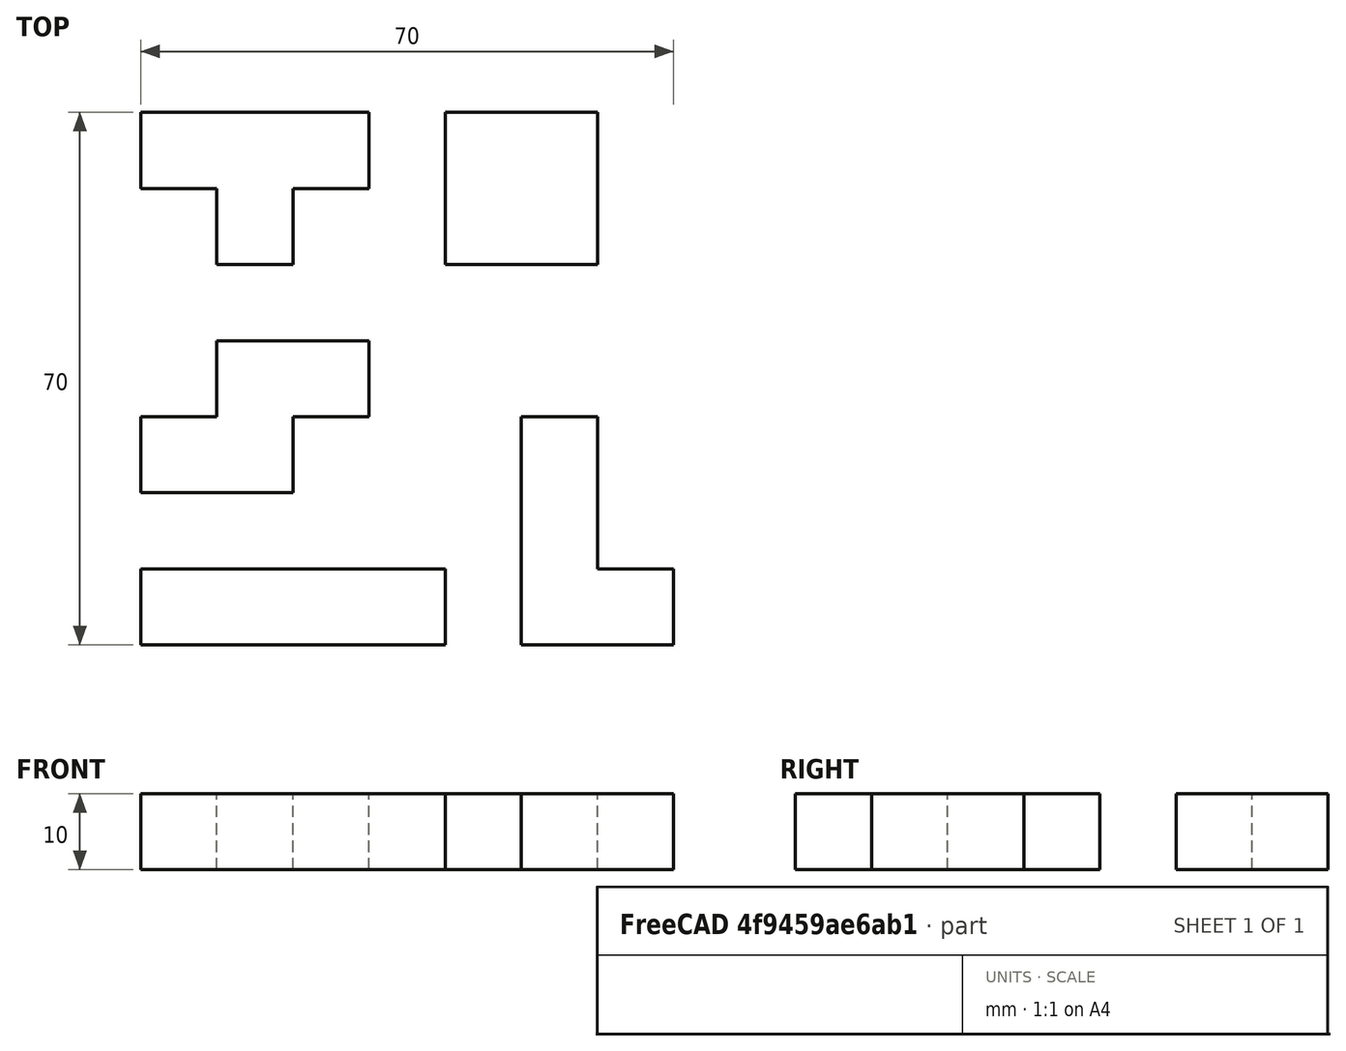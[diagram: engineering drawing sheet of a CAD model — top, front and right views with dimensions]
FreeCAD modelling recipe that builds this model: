
FCSTD DOCUMENT  (FreeCAD 1.0R39285 (Git))
Label: ojt1_t05r03_tetris
License: All rights reserved
objects: Part::Box×20, Part::MultiFuse×5
note: 25 computed .brp shape members not serialized (recipe doc carries the construction recipe); baked Part::Feature solids carry a one-line shape summary decoded from their .brp

FEATURE [Part::Box] Box  label="Cub"
  AttacherType = Attacher::AttachEngine3D
  Height = 10
  Length = 10
  Width = 10
FEATURE [Part::Box] Box001  label="Cub001"
  AttacherType = Attacher::AttachEngine3D
  Height = 10
  Length = 10
  Placement = pos=(10,0,0) rot=(0,0,1;0rad)
  Width = 10
FEATURE [Part::Box] Box002  label="Cub002"
  AttacherType = Attacher::AttachEngine3D
  Height = 10
  Length = 10
  Placement = pos=(20,0,0) rot=(0,0,1;0rad)
  Width = 10
FEATURE [Part::Box] Box003  label="Cub003"
  AttacherType = Attacher::AttachEngine3D
  Height = 10
  Length = 10
  Placement = pos=(30,0,0) rot=(0,0,1;0rad)
  Width = 10
FEATURE [Part::MultiFuse] Fusion  label="vermella"
  Refine = true
  Shapes = -> [Box,Box001,Box002,Box003]
FEATURE [Part::Box] Box004  label="Cub004"
  AttacherType = Attacher::AttachEngine3D
  Height = 10
  Length = 10
  Placement = pos=(0,20,0) rot=(0,0,1;0rad)
  Width = 10
FEATURE [Part::Box] Box005  label="Cub005"
  AttacherType = Attacher::AttachEngine3D
  Height = 10
  Length = 10
  Placement = pos=(10,20,0) rot=(0,0,1;0rad)
  Width = 10
FEATURE [Part::Box] Box006  label="Cub006"
  AttacherType = Attacher::AttachEngine3D
  Height = 10
  Length = 10
  Placement = pos=(10,30,0) rot=(0,0,1;0rad)
  Width = 10
FEATURE [Part::Box] Box007  label="Cub007"
  AttacherType = Attacher::AttachEngine3D
  Height = 10
  Length = 10
  Placement = pos=(20,30,0) rot=(0,0,1;0rad)
  Width = 10
FEATURE [Part::MultiFuse] Fusion001  label="blau_mari"
  Refine = true
  Shapes = -> [Box004,Box005,Box006,Box007]
FEATURE [Part::Box] Box008  label="Cub008"
  AttacherType = Attacher::AttachEngine3D
  Height = 10
  Length = 10
  Placement = pos=(0,60,0) rot=(0,0,1;0rad)
  Width = 10
FEATURE [Part::Box] Box009  label="Cub009"
  AttacherType = Attacher::AttachEngine3D
  Height = 10
  Length = 10
  Placement = pos=(10,60,0) rot=(0,0,1;0rad)
  Width = 10
FEATURE [Part::Box] Box010  label="Cub010"
  AttacherType = Attacher::AttachEngine3D
  Height = 10
  Length = 10
  Placement = pos=(20,60,0) rot=(0,0,1;0rad)
  Width = 10
FEATURE [Part::Box] Box011  label="Cub011"
  AttacherType = Attacher::AttachEngine3D
  Height = 10
  Length = 10
  Placement = pos=(10,50,0) rot=(0,0,1;0rad)
  Width = 10
FEATURE [Part::MultiFuse] Fusion002  label="gris"
  Refine = true
  Shapes = -> [Box008,Box009,Box010,Box011]
FEATURE [Part::Box] Box012  label="Cub012"
  AttacherType = Attacher::AttachEngine3D
  Height = 10
  Length = 10
  Placement = pos=(50,0,0) rot=(0,0,1;0rad)
  Width = 10
FEATURE [Part::Box] Box013  label="Cub013"
  AttacherType = Attacher::AttachEngine3D
  Height = 10
  Length = 10
  Placement = pos=(60,0,0) rot=(0,0,1;0rad)
  Width = 10
FEATURE [Part::Box] Box014  label="Cub014"
  AttacherType = Attacher::AttachEngine3D
  Height = 10
  Length = 10
  Placement = pos=(50,10,0) rot=(0,0,1;0rad)
  Width = 10
FEATURE [Part::Box] Box015  label="Cub015"
  AttacherType = Attacher::AttachEngine3D
  Height = 10
  Length = 10
  Placement = pos=(50,20,0) rot=(0,0,1;0rad)
  Width = 10
FEATURE [Part::MultiFuse] Fusion003  label="groc"
  Refine = true
  Shapes = -> [Box012,Box013,Box014,Box015]
FEATURE [Part::Box] Box016  label="Cub016"
  AttacherType = Attacher::AttachEngine3D
  Height = 10
  Length = 10
  Placement = pos=(40,60,0) rot=(0,0,1;0rad)
  Width = 10
FEATURE [Part::Box] Box017  label="Cub017"
  AttacherType = Attacher::AttachEngine3D
  Height = 10
  Length = 10
  Placement = pos=(50,60,0) rot=(0,0,1;0rad)
  Width = 10
FEATURE [Part::Box] Box018  label="Cub018"
  AttacherType = Attacher::AttachEngine3D
  Height = 10
  Length = 10
  Placement = pos=(40,50,0) rot=(0,0,1;0rad)
  Width = 10
FEATURE [Part::Box] Box019  label="Cub019"
  AttacherType = Attacher::AttachEngine3D
  Height = 10
  Length = 10
  Placement = pos=(50,50,0) rot=(0,0,1;0rad)
  Width = 10
FEATURE [Part::MultiFuse] Fusion004  label="blau_cel"
  Refine = true
  Shapes = -> [Box016,Box017,Box018,Box019]
